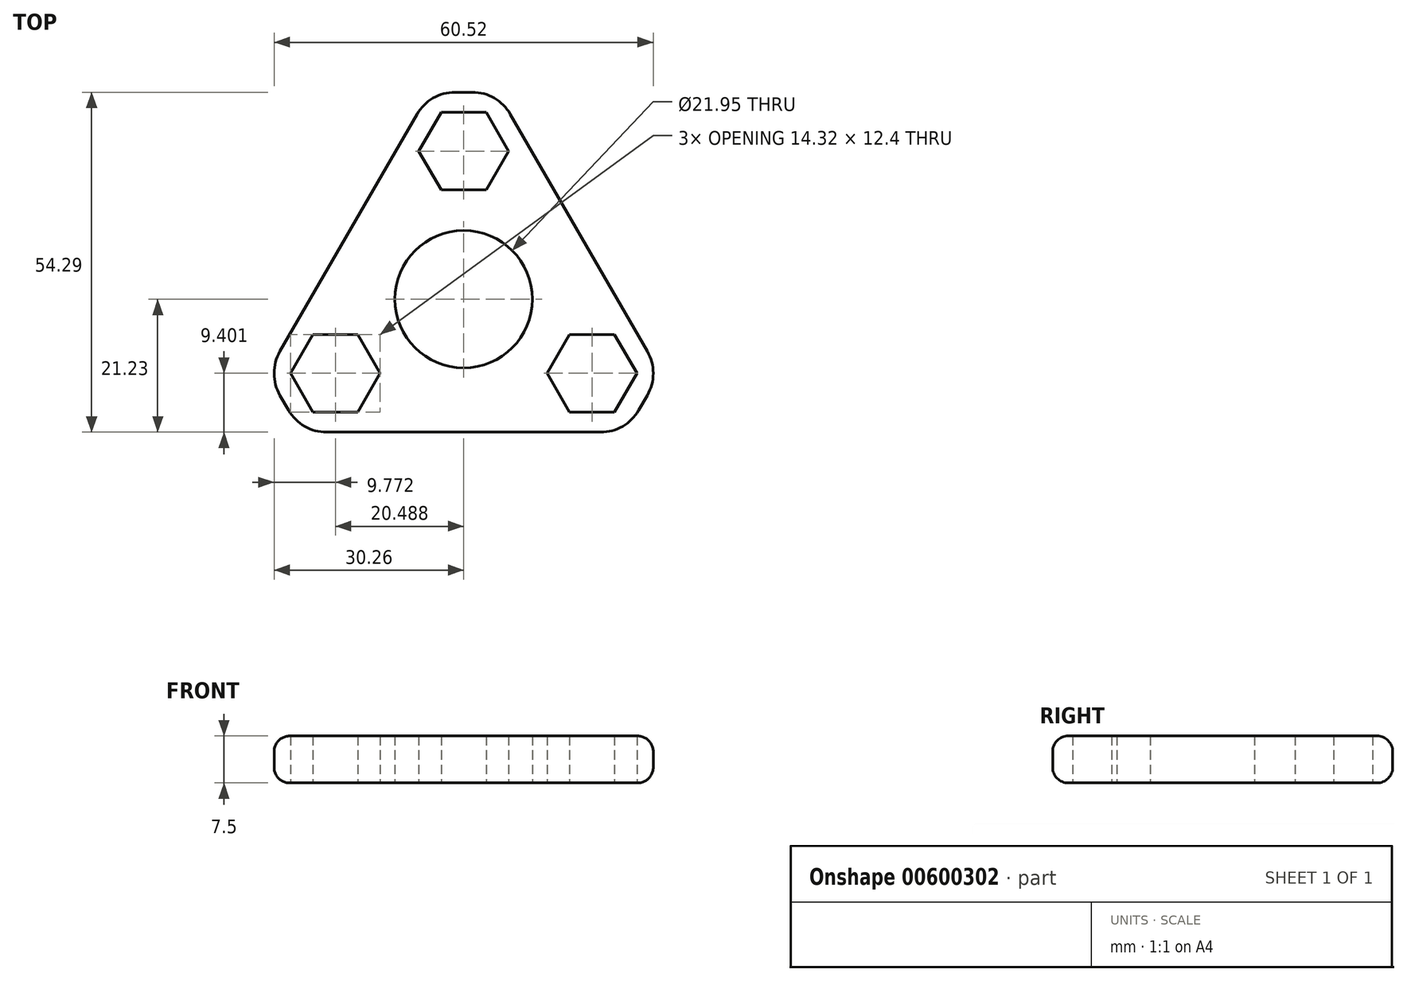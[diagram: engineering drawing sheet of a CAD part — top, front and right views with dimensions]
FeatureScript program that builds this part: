
annotation { "Feature Type Name" : "Feature", "Feature Type Description" : "" }
export const myFeature = defineFeature(function(context is Context, id is Id, definition is map)
    precondition{}
    {
        {
            var Q0;
            Q0=qCreatedBy(makeId("Top.planeOp"),FACE);
            var sketch = newSketch(context, id + "F0", { "sketchPlane" : qUnion([Q0])});
            skCircle(sketch, "E0", {"center": v(0, 0) * mm, "radius": 33.5 * mm, "construction": true});
            skLineSegment(sketch, "E1", {"start": v(0, 23.66) * mm, "end": v(0, 0) * mm, "construction": true});
            skLineSegment(sketch, "E2", {"start": v(0, 0) * mm, "end": v(-20.49, -11.83) * mm, "construction": true});
            skLineSegment(sketch, "E3", {"start": v(0, 0) * mm, "end": v(20.49, -11.83) * mm, "construction": true});
            skCircle(sketch, "E4.cCircle", {"center": v(0, 23.66) * mm, "radius": 6.2 * mm, "construction": true});
            skLineSegment(sketch, "E4.0", {"start": v(7.16, 23.66) * mm, "end": v(3.58, 17.46) * mm});
            skLineSegment(sketch, "E4.1", {"start": v(3.58, 17.46) * mm, "end": v(-3.58, 17.46) * mm});
            skLineSegment(sketch, "E4.2", {"start": v(-3.58, 17.46) * mm, "end": v(-7.16, 23.66) * mm});
            skLineSegment(sketch, "E4.3", {"start": v(-7.16, 23.66) * mm, "end": v(-3.58, 29.86) * mm});
            skLineSegment(sketch, "E4.4", {"start": v(-3.58, 29.86) * mm, "end": v(3.58, 29.86) * mm});
            skLineSegment(sketch, "E4.5", {"start": v(3.58, 29.86) * mm, "end": v(7.16, 23.66) * mm});
            skPoint(sketch, "E4.0.midPoint", {"position": v(5.37, 20.56) * mm});
            skCircle(sketch, "E5.cCircle", {"center": v(0, 23.66) * mm, "radius": 9.4 * mm, "construction": true});
            skLineSegment(sketch, "E5.3", {"start": v(-10.85, 23.66) * mm, "end": v(-5.43, 33.06) * mm});
            skLineSegment(sketch, "E5.4", {"start": v(-5.43, 33.06) * mm, "end": v(5.43, 33.06) * mm});
            skLineSegment(sketch, "E5.5", {"start": v(5.43, 33.06) * mm, "end": v(10.85, 23.66) * mm});
            skCircle(sketch, "E6", {"center": v(0, 0) * mm, "radius": 10.97 * mm});
            skCircle(sketch, "E7.cCircle", {"center": v(20.49, -11.83) * mm, "radius": 6.2 * mm, "construction": true});
            skLineSegment(sketch, "E7.0", {"start": v(27.65, -11.83) * mm, "end": v(24.07, -18.03) * mm});
            skLineSegment(sketch, "E7.1", {"start": v(24.07, -18.03) * mm, "end": v(16.9, -18.03) * mm});
            skLineSegment(sketch, "E7.2", {"start": v(16.9, -18.03) * mm, "end": v(13.33, -11.83) * mm});
            skLineSegment(sketch, "E7.3", {"start": v(13.33, -11.83) * mm, "end": v(16.9, -5.63) * mm});
            skLineSegment(sketch, "E7.4", {"start": v(16.9, -5.63) * mm, "end": v(24.07, -5.63) * mm});
            skLineSegment(sketch, "E7.5", {"start": v(24.07, -5.63) * mm, "end": v(27.65, -11.83) * mm});
            skPoint(sketch, "E7.0.midPoint", {"position": v(25.86, -14.93) * mm});
            skCircle(sketch, "E8.cCircle", {"center": v(20.49, -11.83) * mm, "radius": 9.4 * mm, "construction": true});
            skLineSegment(sketch, "E8.0", {"start": v(31.34, -11.83) * mm, "end": v(25.92, -21.23) * mm});
            skLineSegment(sketch, "E8.1", {"start": v(25.92, -21.23) * mm, "end": v(15.06, -21.23) * mm});
            skLineSegment(sketch, "E8.5", {"start": v(25.92, -2.43) * mm, "end": v(31.34, -11.83) * mm});
            skPoint(sketch, "E8.0.midPoint", {"position": v(28.63, -16.53) * mm});
            skCircle(sketch, "E9.cCircle", {"center": v(-20.49, -11.83) * mm, "radius": 6.2 * mm, "construction": true});
            skLineSegment(sketch, "E9.0", {"start": v(-13.33, -11.83) * mm, "end": v(-16.9, -18.03) * mm});
            skLineSegment(sketch, "E9.1", {"start": v(-16.9, -18.03) * mm, "end": v(-24.07, -18.03) * mm});
            skLineSegment(sketch, "E9.2", {"start": v(-24.07, -18.03) * mm, "end": v(-27.65, -11.83) * mm});
            skLineSegment(sketch, "E9.3", {"start": v(-27.65, -11.83) * mm, "end": v(-24.07, -5.63) * mm});
            skLineSegment(sketch, "E9.4", {"start": v(-24.07, -5.63) * mm, "end": v(-16.9, -5.63) * mm});
            skLineSegment(sketch, "E9.5", {"start": v(-16.9, -5.63) * mm, "end": v(-13.33, -11.83) * mm});
            skPoint(sketch, "E9.0.midPoint", {"position": v(-15.12, -14.93) * mm});
            skCircle(sketch, "E10.cCircle", {"center": v(-20.49, -11.83) * mm, "radius": 9.4 * mm, "construction": true});
            skLineSegment(sketch, "E10.1", {"start": v(-15.06, -21.23) * mm, "end": v(-25.92, -21.23) * mm});
            skLineSegment(sketch, "E10.2", {"start": v(-25.92, -21.23) * mm, "end": v(-31.34, -11.83) * mm});
            skLineSegment(sketch, "E10.3", {"start": v(-31.34, -11.83) * mm, "end": v(-25.92, -2.43) * mm});
            skLineSegment(sketch, "E11", {"start": v(-25.92, -2.43) * mm, "end": v(-10.85, 23.66) * mm});
            skLineSegment(sketch, "E12", {"start": v(10.85, 23.66) * mm, "end": v(25.92, -2.43) * mm});
            skLineSegment(sketch, "E13", {"start": v(15.06, -21.23) * mm, "end": v(-15.06, -21.23) * mm});
            skSolve(sketch);
        }
        {
            var Q0;
            Q0=qSketchRegion(id+"F0",true);
            extrude(context, id + "F1", {"entities" : qUnion([Q0]), "endBound" : BoundingType.SYMMETRIC, "depth" : 7.5 * mm, "offsetDistance" : 25 * mm});
        }
        {
            var Q0;
            Q0=makeQuery(id+"F1.opExtrude","SWEPT_EDGE",EDGE,{"disambiguationData":[OSD([sQuery(id+"F0.wireOp",EDGE,"O4FCEVp2-a76e-EbQX-IVHh-MGuyo65jWMq8"),sQuery(id+"F0.wireOp",EDGE,"C5uhuAOH-5J48-u82k-IHs0-f85elHY0iJHz")])]});
            var Q1;
            Q1=makeQuery(id+"F1.opExtrude","SWEPT_EDGE",EDGE,{"disambiguationData":[OSD([sQuery(id+"F0.wireOp",EDGE,"O4FCEVp2-a76e-EbQX-IVHh-MGuyo65jWMq8"),sQuery(id+"F0.wireOp",EDGE,"S8u6JOnv-uHRI-fFma-sm4u-xtKy3LCOX3hA")])]});
            var Q2;
            Q2=makeQuery(id+"F1.opExtrude","SWEPT_EDGE",EDGE,{"disambiguationData":[OSD([sQuery(id+"F0.wireOp",EDGE,"O4FCEVp2-a76e-EbQX-IVHh-MGuyo65jWMq8"),sQuery(id+"F0.wireOp",EDGE,"SAWo3aZG-HSuV-OBrD-h2Rh-DnAgDfp8ozeu")])]});
            var Q3;
            Q3=makeQuery(id+"F1.opExtrude","SWEPT_EDGE",EDGE,{"disambiguationData":[OSD([sQuery(id+"F0.wireOp",EDGE,"O4FCEVp2-a76e-EbQX-IVHh-MGuyo65jWMq8"),sQuery(id+"F0.wireOp",EDGE,"SbUdLMAy-5HOI-FCRc-lumj-AurxfLcrsVdC")])]});
            var Q4;
            Q4=makeQuery(id+"F1.opExtrude","SWEPT_EDGE",EDGE,{"disambiguationData":[OSD([sQuery(id+"F0.wireOp",EDGE,"O4FCEVp2-a76e-EbQX-IVHh-MGuyo65jWMq8"),sQuery(id+"F0.wireOp",EDGE,"X8zT3j1a-ayFc-XZkv-8J8U-pHVy1uolJ5Bv")])]});
            var Q5;
            Q5=makeQuery(id+"F1.opExtrude","SWEPT_EDGE",EDGE,{"disambiguationData":[OSD([sQuery(id+"F0.wireOp",EDGE,"O4FCEVp2-a76e-EbQX-IVHh-MGuyo65jWMq8"),sQuery(id+"F0.wireOp",EDGE,"QmNcphut-FD3I-4b19-zAlT-9cwEKW2qgaVM")])]});
            var Q6;
            Q6=makeQuery(id+"F1.opExtrude","SWEPT_EDGE",EDGE,{"disambiguationData":[OSD([sQuery(id+"F0.wireOp",EDGE,"E8.4"),sQuery(id+"F0.wireOp",EDGE,"E8.5")])]});
            var Q7;
            Q7=makeQuery(id+"F1.opExtrude","SWEPT_EDGE",EDGE,{"disambiguationData":[OSD([sQuery(id+"F0.wireOp",EDGE,"E8.0"),sQuery(id+"F0.wireOp",EDGE,"E8.5")])]});
            var Q8;
            Q8=makeQuery(id+"F1.opExtrude","SWEPT_EDGE",EDGE,{"disambiguationData":[OSD([sQuery(id+"F0.wireOp",EDGE,"E8.0"),sQuery(id+"F0.wireOp",EDGE,"E8.1")])]});
            var Q9;
            Q9=makeQuery(id+"F1.opExtrude","SWEPT_EDGE",EDGE,{"disambiguationData":[OSD([sQuery(id+"F0.wireOp",EDGE,"E8.1"),sQuery(id+"F0.wireOp",EDGE,"E8.2")])]});
            var Q10;
            Q10=makeQuery(id+"F1.opExtrude","SWEPT_EDGE",EDGE,{"disambiguationData":[OSD([sQuery(id+"F0.wireOp",EDGE,"E10.0"),sQuery(id+"F0.wireOp",EDGE,"E10.1")])]});
            var Q11;
            Q11=makeQuery(id+"F1.opExtrude","SWEPT_EDGE",EDGE,{"disambiguationData":[OSD([sQuery(id+"F0.wireOp",EDGE,"E10.1"),sQuery(id+"F0.wireOp",EDGE,"E10.2")])]});
            var Q12;
            Q12=makeQuery(id+"F1.opExtrude","SWEPT_EDGE",EDGE,{"disambiguationData":[OSD([sQuery(id+"F0.wireOp",EDGE,"E10.2"),sQuery(id+"F0.wireOp",EDGE,"E10.3")])]});
            var Q13;
            Q13=makeQuery(id+"F1.opExtrude","SWEPT_EDGE",EDGE,{"disambiguationData":[OSD([sQuery(id+"F0.wireOp",EDGE,"E10.3"),sQuery(id+"F0.wireOp",EDGE,"E10.4")])]});
            var Q14;
            Q14=makeQuery(id+"F1.opExtrude","SWEPT_EDGE",EDGE,{"disambiguationData":[OSD([sQuery(id+"F0.wireOp",EDGE,"E5.2"),sQuery(id+"F0.wireOp",EDGE,"E5.3")])]});
            var Q15;
            Q15=makeQuery(id+"F1.opExtrude","SWEPT_EDGE",EDGE,{"disambiguationData":[OSD([sQuery(id+"F0.wireOp",EDGE,"E5.3"),sQuery(id+"F0.wireOp",EDGE,"E5.4")])]});
            var Q16;
            Q16=makeQuery(id+"F1.opExtrude","SWEPT_EDGE",EDGE,{"disambiguationData":[OSD([sQuery(id+"F0.wireOp",EDGE,"E5.4"),sQuery(id+"F0.wireOp",EDGE,"E5.5")])]});
            var Q17;
            Q17=makeQuery(id+"F1.opExtrude","SWEPT_EDGE",EDGE,{"disambiguationData":[OSD([sQuery(id+"F0.wireOp",EDGE,"E5.0"),sQuery(id+"F0.wireOp",EDGE,"E5.5")])]});
            fillet(context, id + "F2", {"entities" : qUnion([Q0, Q1, Q2, Q3, Q4, Q5, Q6, Q7, Q8, Q9, Q10, Q11, Q12, Q13, Q14, Q15, Q16, Q17]), "radius" : 7 * mm, "tangentPropagation" : true, "allowEdgeOverflow" : false});
        }
        {
            var Q0;
            Q0=makeQuery(id+"F1.opExtrude","SWEPT_FACE",FACE,{"disambiguationData":[OSD([sQuery(id+"F0.wireOp",EDGE,"E5.3"),sQuery(id+"F0.wireOp",EDGE,"E10.3"),sQuery(id+"F0.wireOp",EDGE,"E11")])]});
            fillet(context, id + "F3", {"entities" : qUnion([Q0]), "radius" : 2.5 * mm, "tangentPropagation" : true, "allowEdgeOverflow" : false});
        }
    });
